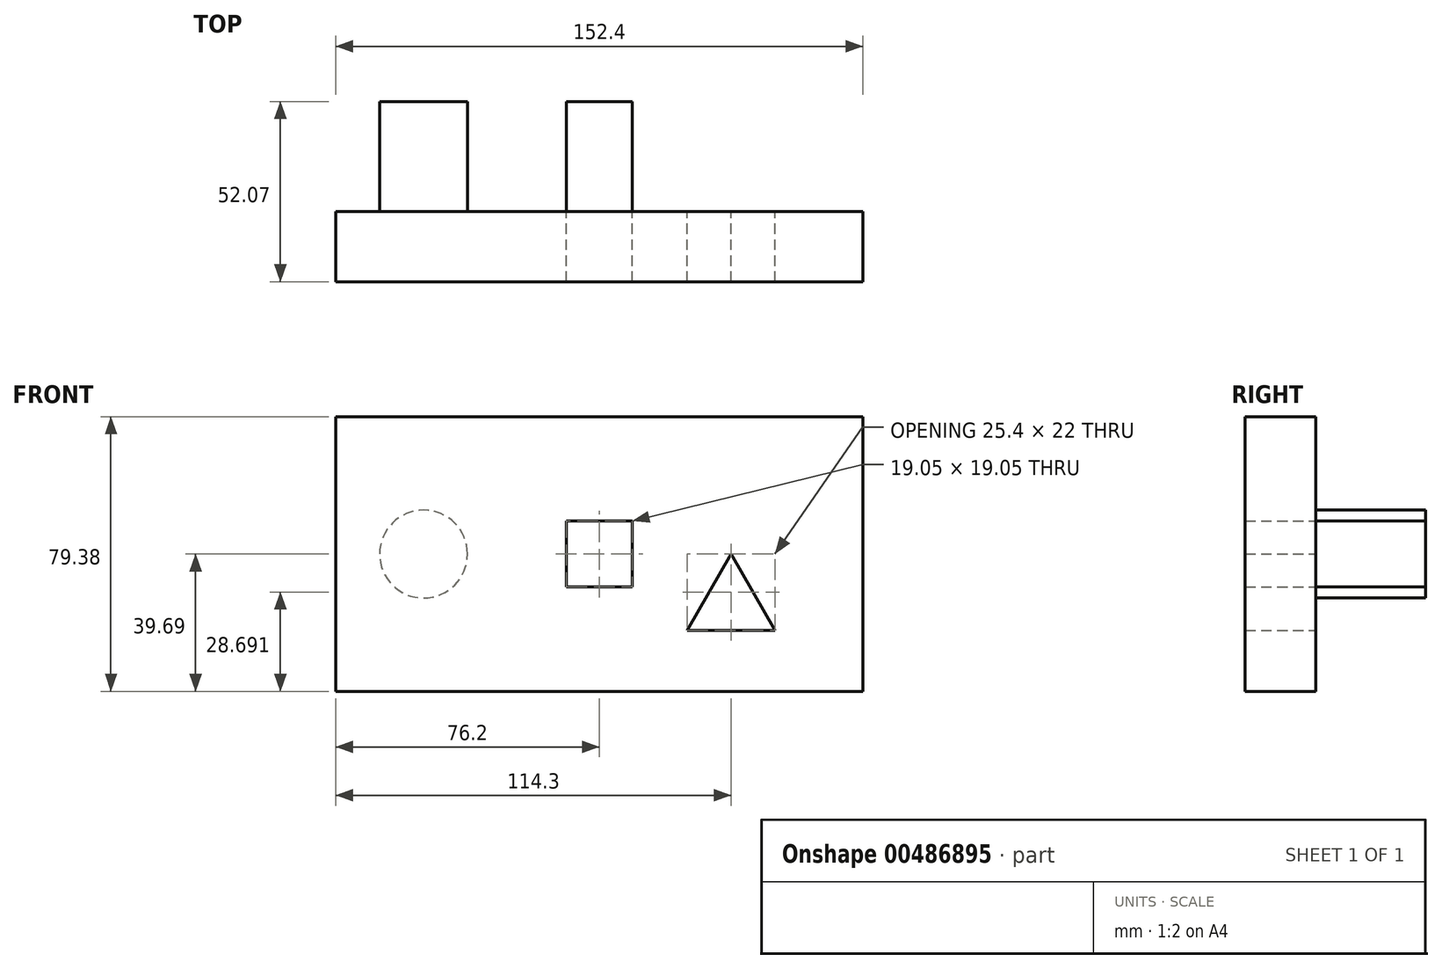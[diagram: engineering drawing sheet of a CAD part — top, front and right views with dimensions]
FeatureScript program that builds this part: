
annotation { "Feature Type Name" : "Feature", "Feature Type Description" : "" }
export const myFeature = defineFeature(function(context is Context, id is Id, definition is map)
    precondition{}
    {
        {
            var Q0;
            Q0=qCreatedBy(makeId("Front.planeOp"),FACE);
            var sketch = newSketch(context, id + "F0", { "sketchPlane" : qUnion([Q0])});
            skLineSegment(sketch, "E0", {"start": v(0, 0) * mm, "end": v(6.35, 0) * mm});
            skLineSegment(sketch, "E1", {"start": v(6.35, 0) * mm, "end": v(-6.35, -22) * mm});
            skLineSegment(sketch, "E2", {"start": v(6.35, 0) * mm, "end": v(19.05, -22) * mm});
            skLineSegment(sketch, "E3", {"start": v(-6.35, -22) * mm, "end": v(19.05, -22) * mm});
            skLineSegment(sketch, "E4", {"start": v(0, 0) * mm, "end": v(-31.75, 0) * mm});
            skLineSegment(sketch, "E5.bottom", {"start": v(-41.28, -9.52) * mm, "end": v(-22.23, -9.52) * mm});
            skLineSegment(sketch, "E5.top", {"start": v(-41.28, 9.53) * mm, "end": v(-22.23, 9.53) * mm});
            skLineSegment(sketch, "E5.left", {"start": v(-41.28, -9.52) * mm, "end": v(-41.28, 9.53) * mm});
            skLineSegment(sketch, "E5.right", {"start": v(-22.22, -9.52) * mm, "end": v(-22.23, 9.53) * mm});
            skPoint(sketch, "E5.middle", {"position": v(-31.75, 0) * mm});
            skLineSegment(sketch, "E6", {"start": v(-31.75, 0) * mm, "end": v(-82.55, 0) * mm});
            skCircle(sketch, "E7", {"center": v(-82.55, 0) * mm, "radius": 12.7 * mm});
            skLineSegment(sketch, "E8", {"start": v(0, 0) * mm, "end": v(44.45, 0) * mm});
            skLineSegment(sketch, "E9", {"start": v(44.45, 39.69) * mm, "end": v(-107.95, 39.69) * mm});
            skLineSegment(sketch, "E10", {"start": v(44.45, -39.69) * mm, "end": v(-107.95, -39.69) * mm});
            skLineSegment(sketch, "E11", {"start": v(-107.95, 39.69) * mm, "end": v(-107.95, -39.69) * mm});
            skLineSegment(sketch, "E12", {"start": v(44.45, 39.69) * mm, "end": v(44.45, -39.69) * mm});
            skSolve(sketch);
        }
        {
            var Q0;
            Q0 = qSketchRegion(id + "F0", true);
            var Q1;
            Q1=makeQuery(id+"F0.imprint","IMPRINT",FACE,{"disambiguationData":[TD([[makeQuery(id+"F0.imprint","IMPRINT",EDGE,{"derivedFrom":sQuery(id+"F0.wireOp",EDGE,"E7")}),1.0]])]});
            extrude(context, id + "F1", {"entities" : qUnion([Q0, Q1]), "depth" : 20.32 * mm});
        }
        {
            var Q0;
            Q0=makeQuery(id+"F0.imprint","IMPRINT",FACE,{"disambiguationData":[TD([[makeQuery(id+"F0.imprint","IMPRINT",EDGE,{"derivedFrom":sQuery(id+"F0.wireOp",EDGE,"E7")}),1.0]])]});
            extrude(context, id + "F2", {"entities" : qUnion([Q0]), "operationType" : NewBodyOperationType.ADD, "depth" : -31.75 * mm});
        }
        {
            var Q0;
            {var subQ1=sQuery(id+"F0.wireOp",EDGE,"E5.top");Q0=makeQuery(id+"F0.imprint","IMPRINT",FACE,{"disambiguationData":[TD([[makeQuery(id+"F0.imprint","IMPRINT",EDGE,{"derivedFrom":subQ1}),-1.0]])]});}
            var Q1;
            {var subQ1=sQuery(id+"F0.wireOp",EDGE,"E5.bottom");Q1=makeQuery(id+"F0.imprint","IMPRINT",FACE,{"disambiguationData":[TD([[makeQuery(id+"F0.imprint","IMPRINT",EDGE,{"derivedFrom":subQ1}),1.0]])]});}
            extrude(context, id + "F3", {"entities" : qUnion([Q0, Q1]), "operationType" : NewBodyOperationType.ADD, "oppositeDirection" : true, "depth" : 31.75 * mm});
        }
    });
